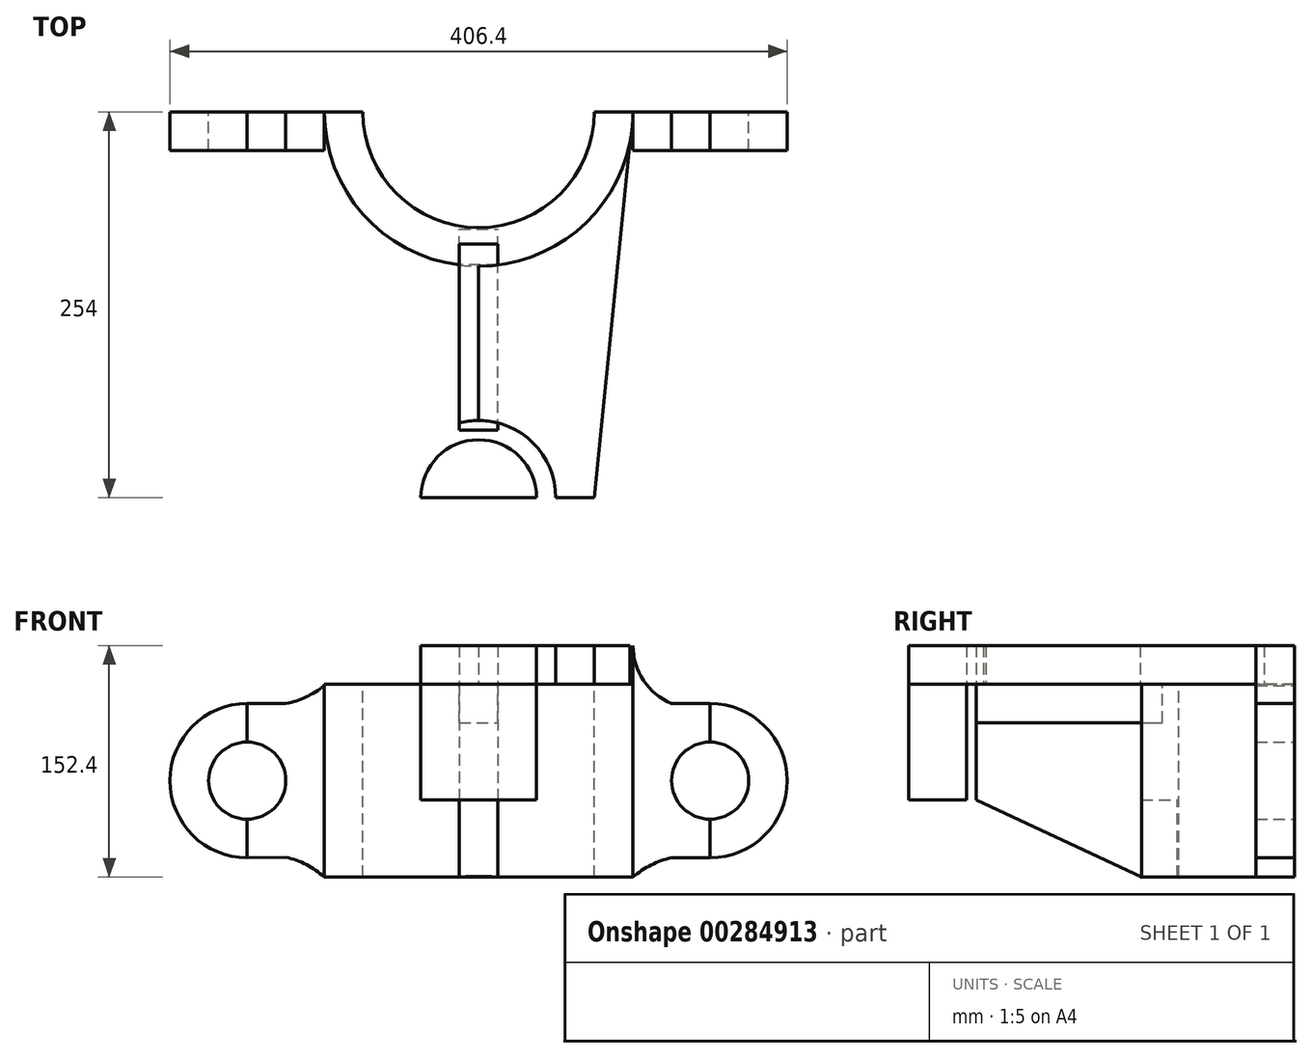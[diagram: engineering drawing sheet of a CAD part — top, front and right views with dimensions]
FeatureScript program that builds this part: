
annotation { "Feature Type Name" : "Feature", "Feature Type Description" : "" }
export const myFeature = defineFeature(function(context is Context, id is Id, definition is map)
    precondition{}
    {
        {
            var Q0;
            Q0=qCreatedBy(makeId("Front.planeOp"),FACE);
            var sketch = newSketch(context, id + "F0", { "sketchPlane" : qUnion([Q0])});
            skLineSegment(sketch, "E0.bottom", {"start": v(-101.6, 63.5) * mm, "end": v(101.6, 63.5) * mm});
            skLineSegment(sketch, "E0.top", {"start": v(-101.6, -63.5) * mm, "end": v(101.6, -63.5) * mm});
            skLineSegment(sketch, "E0.left", {"start": v(-101.6, 63.5) * mm, "end": v(-101.6, -63.5) * mm});
            skLineSegment(sketch, "E0.right", {"start": v(101.6, 63.5) * mm, "end": v(101.6, -63.5) * mm});
            skPoint(sketch, "E0.middle", {"position": v(0, 0) * mm});
            skLineSegment(sketch, "E1.left", {"start": v(101.6, 63.4) * mm, "end": v(101.6, -63.6) * mm});
            skLineSegment(sketch, "E1.right", {"start": v(152.4, 63.4) * mm, "end": v(152.4, -63.6) * mm});
            skLineSegment(sketch, "E2.bottom", {"start": v(-101.6, 62.59) * mm, "end": v(-152.4, 62.59) * mm});
            skLineSegment(sketch, "E2.top", {"start": v(-101.6, -64.41) * mm, "end": v(-152.4, -64.41) * mm});
            skLineSegment(sketch, "E2.left", {"start": v(-101.6, 62.59) * mm, "end": v(-101.6, -64.41) * mm});
            skLineSegment(sketch, "E2.right", {"start": v(-152.4, 62.59) * mm, "end": v(-152.4, -64.41) * mm});
            skLineSegment(sketch, "E3.bottom", {"start": v(152.4, 50.8) * mm, "end": v(203.2, 50.8) * mm});
            skLineSegment(sketch, "E3.top", {"start": v(152.4, -50.8) * mm, "end": v(203.2, -50.8) * mm});
            skLineSegment(sketch, "E3.left", {"start": v(152.4, 50.8) * mm, "end": v(152.4, -50.8) * mm});
            skLineSegment(sketch, "E3.right", {"start": v(203.2, 50.8) * mm, "end": v(203.2, -50.8) * mm});
            skLineSegment(sketch, "E4.bottom", {"start": v(-152.4, 50.8) * mm, "end": v(-203.2, 50.8) * mm});
            skLineSegment(sketch, "E4.top", {"start": v(-152.4, -50.8) * mm, "end": v(-203.2, -50.8) * mm});
            skLineSegment(sketch, "E4.right", {"start": v(-203.2, 50.8) * mm, "end": v(-203.2, -50.8) * mm});
            skPoint(sketch, "E5", {"position": v(-203.2, 0) * mm});
            skPoint(sketch, "E6", {"position": v(203.2, 0) * mm});
            skLineSegment(sketch, "E7", {"start": v(-152.4, 50.8) * mm, "end": v(-152.4, -50.8) * mm});
            skLineSegment(sketch, "E8", {"start": v(152.4, -50.8) * mm, "end": v(152.4, 50.8) * mm});
            skPoint(sketch, "E9", {"position": v(-127, 62.59) * mm});
            skPoint(sketch, "E10", {"position": v(-127, -64.41) * mm});
            skLineSegment(sketch, "E11", {"start": v(-127, 62.59) * mm, "end": v(-127, -64.41) * mm});
            skPoint(sketch, "E12", {"position": v(127, 63.4) * mm});
            skPoint(sketch, "E13", {"position": v(127, -63.6) * mm});
            skLineSegment(sketch, "E14", {"start": v(127, 63.4) * mm, "end": v(127, -63.6) * mm});
            skLineSegment(sketch, "E15", {"start": v(101.6, 63.5) * mm, "end": v(127, 63.4) * mm});
            skLineSegment(sketch, "E16", {"start": v(101.6, -63.5) * mm, "end": v(127, -63.6) * mm});
            skLineSegment(sketch, "E17", {"start": v(127, 63.4) * mm, "end": v(152.4, 63.4) * mm});
            skLineSegment(sketch, "E18", {"start": v(127, -63.6) * mm, "end": v(152.4, -63.6) * mm});
            skSolve(sketch);
        }
        {
            var Q0;
            Q0=makeQuery(id+"F0.imprint","IMPRINT",FACE,{"disambiguationData":[TD([[makeQuery(id+"F0.imprint","IMPRINT",EDGE,{"derivedFrom":sQuery(id+"F0.wireOp",EDGE,"E3.bottom")}),-1.0]])]});
            var Q1;
            Q1=makeQuery(id+"F0.imprint","IMPRINT",FACE,{"disambiguationData":[TD([[makeQuery(id+"F0.imprint","IMPRINT",EDGE,{"derivedFrom":sQuery(id+"F0.wireOp",EDGE,"E4.bottom")}),1.0]])]});
            extrude(context, id + "F1", {"entities" : qUnion([Q0, Q1]), "depth" : 25.4 * mm});
        }
        {
            var Q0;
            Q0=makeQuery(id+"F1.opExtrude","SWEPT_EDGE",EDGE,{"disambiguationData":[OSD([sQuery(id+"F0.wireOp",EDGE,"E4.bottom"),sQuery(id+"F0.wireOp",EDGE,"E4.right")])]});
            var Q1;
            Q1=makeQuery(id+"F1.opExtrude","SWEPT_EDGE",EDGE,{"disambiguationData":[OSD([sQuery(id+"F0.wireOp",EDGE,"E4.top"),sQuery(id+"F0.wireOp",EDGE,"E4.right")])]});
            var Q2;
            Q2=makeQuery(id+"F1.opExtrude","SWEPT_EDGE",EDGE,{"disambiguationData":[OSD([sQuery(id+"F0.wireOp",EDGE,"E3.top"),sQuery(id+"F0.wireOp",EDGE,"E3.right")])]});
            var Q3;
            Q3=makeQuery(id+"F1.opExtrude","SWEPT_EDGE",EDGE,{"disambiguationData":[OSD([sQuery(id+"F0.wireOp",EDGE,"E3.bottom"),sQuery(id+"F0.wireOp",EDGE,"E3.right")])]});
            fillet(context, id + "F2", {"entities" : qUnion([Q0, Q1, Q2, Q3]), "radius" : 50.8 * mm, "tangentPropagation" : true, "allowEdgeOverflow" : false});
        }
        {
            var Q0;
            Q0=makeQuery(id+"F0.imprint","IMPRINT",FACE,{"disambiguationData":[TD([[makeQuery(id+"F0.imprint","IMPRINT",EDGE,{"derivedFrom":sQuery(id+"F0.wireOp",EDGE,"E0.bottom")}),-1.0]])]});
            var sketch = newSketch(context, id + "F3", { "sketchPlane" : qUnion([Q0])});
            skSolve(sketch);
        }
        {
            var Q0;
            Q0=makeQuery(id+"F0.imprint","IMPRINT",FACE,{"disambiguationData":[TD([[makeQuery(id+"F0.imprint","IMPRINT",EDGE,{"derivedFrom":sQuery(id+"F0.wireOp",EDGE,"E0.bottom")}),-1.0]])]});
            var sketch = newSketch(context, id + "F4", { "sketchPlane" : qUnion([Q0])});
            skArc(sketch, "E19", {"start": v(-127, 50.8) * mm, "mid": v(-113.57, 55.12) * mm, "end": v(-101.6, 62.59) * mm});
            skArc(sketch, "E20", {"start": v(127, -50.8) * mm, "mid": v(113.5, -55.55) * mm, "end": v(101.6, -63.5) * mm});
            skArc(sketch, "E21", {"start": v(-101.6, -63.5) * mm, "mid": v(-113.47, -55.34) * mm, "end": v(-127, -50.4) * mm});
            skLineSegment(sketch, "E22", {"start": v(-152.4, 50.8) * mm, "end": v(-127, 50.8) * mm});
            skLineSegment(sketch, "E23", {"start": v(-152.4, -50.8) * mm, "end": v(-127, -50.4) * mm});
            skLineSegment(sketch, "E24", {"start": v(152.4, -50.8) * mm, "end": v(127, -50.8) * mm});
            skLineSegment(sketch, "E25", {"start": v(-152.4, 50.8) * mm, "end": v(-152.4, -50.8) * mm});
            skLineSegment(sketch, "E26", {"start": v(-101.6, 62.59) * mm, "end": v(-101.6, -63.5) * mm});
            skPoint(sketch, "E27", {"position": v(101.6, 88.9) * mm});
            skLineSegment(sketch, "E28", {"start": v(101.6, 88.9) * mm, "end": v(101.6, -63.5) * mm});
            skLineSegment(sketch, "E29", {"start": v(152.4, 50.8) * mm, "end": v(127, 50.8) * mm});
            skArc(sketch, "E30", {"start": v(101.6, 88.9) * mm, "mid": v(108.53, 66) * mm, "end": v(127, 50.8) * mm});
            skLineSegment(sketch, "E31", {"start": v(152.4, 50.8) * mm, "end": v(152.4, -50.8) * mm});
            skSolve(sketch);
        }
        {
            var Q0;
            Q0 = qSketchRegion(id + "F4", true);
            extrude(context, id + "F5", {"entities" : qUnion([Q0]), "depth" : 25.4 * mm});
        }
        {
            var Q0;
            Q0 = qSketchRegion(id + "F3", true);
            var Q1;
            Q1=makeQuery(id+"F3.imprint","IMPRINT",FACE,{"disambiguationData":[TD([[makeQuery(id+"F3.imprint","IMPRINT",EDGE,{"derivedFrom":makeQuery(id+"F0.imprint","IMPRINT",EDGE,{"derivedFrom":sQuery(id+"F0.wireOp",EDGE,"E0.bottom")})}),-1.0]])]});
            extrude(context, id + "F6", {"entities" : qUnion([Q0, Q1]), "depth" : 101.6 * mm});
        }
        {
            var Q0;
            Q0=qCreatedBy(makeId("Front.planeOp"),FACE);
            var sketch = newSketch(context, id + "F7", { "sketchPlane" : qUnion([Q0])});
            skCircle(sketch, "E32", {"center": v(-152.4, 0) * mm, "radius": 25.4 * mm});
            skCircle(sketch, "E33", {"center": v(152.4, 0) * mm, "radius": 25.4 * mm});
            skSolve(sketch);
        }
        {
            var Q0;
            Q0=makeQuery(id+"F7.imprint","IMPRINT",FACE,{"disambiguationData":[TD([[makeQuery(id+"F7.imprint","IMPRINT",EDGE,{"derivedFrom":sQuery(id+"F7.wireOp",EDGE,"E33")}),1.0]])]});
            extrude(context, id + "F8", {"entities" : qUnion([Q0]), "operationType" : NewBodyOperationType.REMOVE, "depth" : 25.4 * mm});
        }
        {
            var Q0;
            Q0=makeQuery(id+"F7.imprint","IMPRINT",FACE,{"disambiguationData":[TD([[makeQuery(id+"F7.imprint","IMPRINT",EDGE,{"derivedFrom":sQuery(id+"F7.wireOp",EDGE,"E32")}),1.0]])]});
            extrude(context, id + "F9", {"entities" : qUnion([Q0]), "operationType" : NewBodyOperationType.REMOVE, "depth" : 25.4 * mm});
        }
        {
            var Q0;
            Q0=makeQuery(id+"F6.opExtrude","CAP_EDGE",EDGE,{"disambiguationData":[OSD([sQuery(id+"F0.wireOp",EDGE,"E0.right"),sQuery(id+"F0.wireOp",EDGE,"E1.left")])],"isStart":false});
            var Q1;
            Q1=makeQuery(id+"F6.opExtrude","CAP_EDGE",EDGE,{"disambiguationData":[OSD([sQuery(id+"F0.wireOp",EDGE,"E0.left"),sQuery(id+"F0.wireOp",EDGE,"E2.left")])],"isStart":false});
            fillet(context, id + "F10", {"entities" : qUnion([Q0, Q1]), "radius" : 101.6 * mm, "tangentPropagation" : true, "allowEdgeOverflow" : false});
        }
        {
            var Q0;
            Q0=qCreatedBy(makeId("Top.planeOp"),FACE);
            var sketch = newSketch(context, id + "F11", { "sketchPlane" : qUnion([Q0])});
            skArc(sketch, "E34", {"start": v(-76.2, 0) * mm, "mid": v(0, -76.2) * mm, "end": v(76.2, 0) * mm});
            skLineSegment(sketch, "E35", {"start": v(-76.2, 0) * mm, "end": v(76.2, 0) * mm});
            skSolve(sketch);
        }
        {
            var Q0;
            Q0 = qSketchRegion(id + "F11", true);
            extrude(context, id + "F12", {"entities" : qUnion([Q0]), "operationType" : NewBodyOperationType.REMOVE, "endBound" : BoundingType.SYMMETRIC, "oppositeDirection" : true, "depth" : 127 * mm});
        }
        {
            var Q0;
            Q0=makeQuery(id+"F6.opExtrude","SWEPT_FACE",FACE,{"disambiguationData":[OSD([sQuery(id+"F0.wireOp",EDGE,"E0.bottom")])]});
            var sketch = newSketch(context, id + "F13", { "sketchPlane" : qUnion([Q0])});
            skPoint(sketch, "E36", {"position": v(0, 0) * mm});
            skPoint(sketch, "E37", {"position": v(101.6, 0) * mm});
            skLineSegment(sketch, "E38", {"start": v(101.6, 0) * mm, "end": v(0, 0) * mm});
            skLineSegment(sketch, "E39", {"start": v(0, -254) * mm, "end": v(0, 0) * mm});
            skLineSegment(sketch, "E40", {"start": v(0, -254) * mm, "end": v(76.2, -254) * mm});
            skLineSegment(sketch, "E41", {"start": v(76.2, -254) * mm, "end": v(101.6, 0) * mm});
            skPoint(sketch, "E42", {"position": v(0, -101.6) * mm});
            skSolve(sketch);
        }
        {
            var Q0;
            {var subQ0=sQuery(id+"F13.wireOp",EDGE,"E40");Q0=makeQuery(id+"F13.imprint","IMPRINT",FACE,{"disambiguationData":[TD([[makeQuery(id+"F13.imprint","IMPRINT",EDGE,{"derivedFrom":subQ0}),1.0]])]});}
            var Q1;
            {var subQ1=sQuery(id+"F13.wireOp",EDGE,"E38");var subQ7=makeQuery(id+"F12.boolean.opBoolean","COPY",EDGE,{"derivedFrom":makeQuery(id+"F12.opExtrude","CAP_EDGE",EDGE,{"disambiguationData":[OSD([sQuery(id+"F11.wireOp",EDGE,"E34")])],"isStart":true})});var subQ9=makeQuery(id+"F13.imprint","INTERSECT",VERTEX,{"derivedFrom":[subQ7,subQ1]});Q1=makeQuery(id+"F13.imprint","IMPRINT",FACE,{"disambiguationData":[TD([[makeQuery(id+"F13.imprint","IMPRINT",EDGE,{"disambiguationData":[TD([[subQ9,1.0]])],"derivedFrom":subQ7}),-1.0]])]});}
            extrude(context, id + "F14", {"entities" : qUnion([Q0, Q1]), "operationType" : NewBodyOperationType.ADD, "depth" : 25.4 * mm});
        }
        {
            var Q0;
            Q0=makeQuery(id+"F14.opExtrude","CAP_FACE",FACE,{"disambiguationData":[OSD([sQuery(id+"F11.wireOp",EDGE,"E34"),sQuery(id+"F13.wireOp",EDGE,"E38"),sQuery(id+"F13.wireOp",EDGE,"E39"),sQuery(id+"F13.wireOp",EDGE,"E40"),sQuery(id+"F13.wireOp",EDGE,"E41")])],"isStart":true});
            var sketch = newSketch(context, id + "F15", { "sketchPlane" : qUnion([Q0])});
            skPoint(sketch, "E43", {"position": v(-98.8, 152.4) * mm});
            skPoint(sketch, "E44", {"position": v(0, 101.6) * mm});
            skLineSegment(sketch, "E45", {"start": v(0, 101.6) * mm, "end": v(0, 177.8) * mm});
            skLineSegment(sketch, "E46", {"start": v(0, 254) * mm, "end": v(0, 254) * mm});
            skArc(sketch, "E47", {"start": v(-50.8, 254) * mm, "mid": v(0, 203.2) * mm, "end": v(50.8, 254) * mm});
            skLineSegment(sketch, "E48", {"start": v(-50.8, 254) * mm, "end": v(50.8, 254) * mm});
            skSolve(sketch);
        }
        {
            var Q0;
            {var subQ0=sQuery(id+"F15.wireOp",EDGE,"E48");var subQ1=sQuery(id+"F15.wireOp",EDGE,"E47");var subQ2=sQuery(id+"F13.wireOp",EDGE,"E40");var subQ3=makeQuery(id+"F15.imprint","INTERSECT",VERTEX,{"derivedFrom":[makeQuery(id+"F14.opExtrude","CAP_EDGE",EDGE,{"disambiguationData":[OSD([subQ2])],"isStart":true}),subQ1,subQ0]});Q0=makeQuery(id+"F15.imprint","IMPRINT",FACE,{"disambiguationData":[TD([[makeQuery(id+"F15.imprint","IMPRINT",EDGE,{"disambiguationData":[TD([[subQ3,1.0]])],"derivedFrom":subQ1}),1.0]])]});}
            extrude(context, id + "F16", {"entities" : qUnion([Q0]), "operationType" : NewBodyOperationType.REMOVE, "oppositeDirection" : true, "depth" : 25.4 * mm});
        }
        {
            var Q0;
            {var subQ0=sQuery(id+"F15.wireOp",EDGE,"E48");var subQ1=sQuery(id+"F15.wireOp",EDGE,"E47");var subQ2=sQuery(id+"F13.wireOp",EDGE,"E40");var subQ3=makeQuery(id+"F15.imprint","INTERSECT",VERTEX,{"derivedFrom":[makeQuery(id+"F14.opExtrude","CAP_EDGE",EDGE,{"disambiguationData":[OSD([subQ2])],"isStart":true}),subQ1,subQ0]});Q0=makeQuery(id+"F15.imprint","IMPRINT",FACE,{"disambiguationData":[TD([[makeQuery(id+"F15.imprint","IMPRINT",EDGE,{"disambiguationData":[TD([[subQ3,1.0]])],"derivedFrom":subQ1}),1.0]])]});}
            var Q1;
            {var subQ0=sQuery(id+"F15.wireOp",EDGE,"E48");var subQ1=sQuery(id+"F15.wireOp",EDGE,"E47");var subQ2=makeQuery(id+"F15.imprint","INTERSECT",VERTEX,{"derivedFrom":[subQ1,subQ0]});Q1=makeQuery(id+"F15.imprint","IMPRINT",FACE,{"disambiguationData":[TD([[makeQuery(id+"F15.imprint","IMPRINT",EDGE,{"disambiguationData":[TD([[subQ2,-1.0]])],"derivedFrom":subQ1}),1.0]])]});}
            extrude(context, id + "F17", {"entities" : qUnion([Q0, Q1]), "operationType" : NewBodyOperationType.ADD, "depth" : 76.2 * mm});
        }
        {
            var Q0;
            {var subQ12=sQuery(id+"F15.wireOp",EDGE,"E45");Q0=makeQuery(id+"F15.imprint","IMPRINT",FACE,{"disambiguationData":[TD([[makeQuery(id+"F15.imprint","IMPRINT",EDGE,{"derivedFrom":subQ12}),1.0]])]});}
            var sketch = newSketch(context, id + "F18", { "sketchPlane" : qUnion([Q0])});
            skLineSegment(sketch, "E49", {"start": v(0, 203.2) * mm, "end": v(0, 98.4) * mm});
            skLineSegment(sketch, "E50", {"start": v(12.7, 87.05) * mm, "end": v(-12.7, 87.05) * mm});
            skPoint(sketch, "E51", {"position": v(0, 209.6) * mm});
            skLineSegment(sketch, "E52", {"start": v(-12.7, 209.6) * mm, "end": v(12.7, 209.6) * mm});
            skLineSegment(sketch, "E53", {"start": v(-12.7, 209.6) * mm, "end": v(-12.7, 87.05) * mm});
            skLineSegment(sketch, "E54", {"start": v(12.7, 209.6) * mm, "end": v(12.7, 87.05) * mm});
            skSolve(sketch);
        }
        {
            var Q0;
            Q0 = qSketchRegion(id + "F18", true);
            extrude(context, id + "F19", {"entities" : qUnion([Q0]), "depth" : 25.4 * mm});
        }
        {
            var Q0;
            Q0 = qSketchRegion(id + "F18", true);
            extrude(context, id + "F20", {"entities" : qUnion([Q0]), "depth" : 76.2 * mm});
        }
        {
            var Q0;
            Q0=makeQuery(id+"F20.opExtrude","SWEPT_FACE",FACE,{"disambiguationData":[OSD([sQuery(id+"F18.wireOp",EDGE,"E53")])]});
            var sketch = newSketch(context, id + "F21", { "sketchPlane" : qUnion([Q0])});
            skPoint(sketch, "E55", {"position": v(209.6, -12.7) * mm});
            skLineSegment(sketch, "E56", {"start": v(77.1, -79.06) * mm, "end": v(77.1, -12.7) * mm});
            skLineSegment(sketch, "E57", {"start": v(100.8, -12.7) * mm, "end": v(100.8, -63.5) * mm});
            skLineSegment(sketch, "E58", {"start": v(100.8, -12.7) * mm, "end": v(77.1, -12.7) * mm});
            skLineSegment(sketch, "E59", {"start": v(77.1, -79.06) * mm, "end": v(100.8, -63.5) * mm});
            skLineSegment(sketch, "E60", {"start": v(209.6, -12.7) * mm, "end": v(100.8, -12.7) * mm});
            skLineSegment(sketch, "E61", {"start": v(209.6, -12.7) * mm, "end": v(100.8, -63.5) * mm});
            skSolve(sketch);
        }
        {
            var Q0;
            Q0 = qSketchRegion(id + "F21", true);
            extrude(context, id + "F22", {"entities" : qUnion([Q0]), "operationType" : NewBodyOperationType.ADD, "oppositeDirection" : true, "depth" : 25.4 * mm});
        }
        {
            var Q0;
            Q0=makeQuery(id+"F17.opExtrude","CAP_FACE",FACE,{"disambiguationData":[OSD([sQuery(id+"F15.wireOp",EDGE,"E47"),sQuery(id+"F15.wireOp",EDGE,"E48")])],"isStart":false});
            var sketch = newSketch(context, id + "F23", { "sketchPlane" : qUnion([Q0])});
            skArc(sketch, "E62", {"start": v(38.1, 254) * mm, "mid": v(0, 215.9) * mm, "end": v(-38.1, 254) * mm});
            skLineSegment(sketch, "E63", {"start": v(-38.1, 254) * mm, "end": v(38.1, 254) * mm});
            skSolve(sketch);
        }
        {
            var Q0;
            {var subQ0=sQuery(id+"F15.wireOp",EDGE,"E48");var subQ1=sQuery(id+"F15.wireOp",EDGE,"E47");var subQ2=makeQuery(id+"F15.imprint","INTERSECT",VERTEX,{"derivedFrom":[subQ1,subQ0]});Q0=makeQuery(id+"F15.imprint","IMPRINT",FACE,{"disambiguationData":[TD([[makeQuery(id+"F15.imprint","IMPRINT",EDGE,{"disambiguationData":[TD([[subQ2,-1.0]])],"derivedFrom":subQ1}),1.0]])]});}
            var Q1;
            {var subQ0=sQuery(id+"F15.wireOp",EDGE,"E48");var subQ1=sQuery(id+"F15.wireOp",EDGE,"E47");var subQ2=sQuery(id+"F13.wireOp",EDGE,"E40");var subQ3=makeQuery(id+"F15.imprint","INTERSECT",VERTEX,{"derivedFrom":[makeQuery(id+"F14.opExtrude","CAP_EDGE",EDGE,{"disambiguationData":[OSD([subQ2])],"isStart":true}),subQ1,subQ0]});Q1=makeQuery(id+"F15.imprint","IMPRINT",FACE,{"disambiguationData":[TD([[makeQuery(id+"F15.imprint","IMPRINT",EDGE,{"disambiguationData":[TD([[subQ3,1.0]])],"derivedFrom":subQ1}),1.0]])]});}
            extrude(context, id + "F24", {"entities" : qUnion([Q0, Q1]), "oppositeDirection" : true, "depth" : 25.4 * mm});
        }
        {
            var Q0;
            Q0=makeQuery(id+"F23.imprint","IMPRINT",FACE,{"disambiguationData":[TD([[makeQuery(id+"F23.imprint","IMPRINT",EDGE,{"derivedFrom":sQuery(id+"F23.wireOp",EDGE,"E62")}),-1.0]])]});
            extrude(context, id + "F25", {"entities" : qUnion([Q0]), "operationType" : NewBodyOperationType.REMOVE, "endBound" : BoundingType.THROUGH_ALL, "oppositeDirection" : true, "depth" : 152.4 * mm});
        }
        {
            var Q0;
            {var subQ3=sQuery(id+"F21.wireOp",EDGE,"E57");Q0=makeQuery(id+"F21.imprint","IMPRINT",FACE,{"disambiguationData":[TD([[makeQuery(id+"F21.imprint","IMPRINT",EDGE,{"derivedFrom":subQ3}),-1.0]])]});}
            extrude(context, id + "F26", {"entities" : qUnion([Q0]), "operationType" : NewBodyOperationType.REMOVE, "oppositeDirection" : true, "depth" : 25.4 * mm});
        }
    });
